FCSTD DOCUMENT  (FreeCAD 0.20R29177 +426 (Git))
Label: mechanism-sketch
License: All rights reserved
LicenseURL: http://en.wikipedia.org/wiki/All_rights_reserved
objects: Sketcher::SketchObject×1, PartDesign::Body×1
note: 2 computed .brp shape members not serialized (recipe doc carries the construction recipe); baked Part::Feature solids carry a one-line shape summary decoded from their .brp

FEATURE [Sketcher::SketchObject] Sketch
  FullyConstrained = false
  MapMode = 5
  Support = -> [XY_Plane]
  sketch-geometry (5):
    g0: LineSegment StartX=0 StartY=0 StartZ=0 EndX=77.25 EndY=-20.795 EndZ=0
    g1: LineSegment StartX=0 StartY=-310.679 StartZ=0 EndX=77.25 EndY=-20.795 EndZ=0
    g2: LineSegment StartX=0 StartY=0 StartZ=0 EndX=-77.25 EndY=20.795 EndZ=0
    g3: LineSegment StartX=-77.25 StartY=20.795 StartZ=0 EndX=-154.5 EndY=-269.088 EndZ=0
    g4: LineSegment StartX=0 StartY=-310.679 StartZ=0 EndX=-154.5 EndY=-269.088 EndZ=0
  constraints (13):
    c: Coincident(g0,g-1)
    c: PointOnObject(g1,g-2)
    c: Coincident(g1,g0)
    c: Distance(g0) = 80
    c: Distance(g1) = 300
    c: Coincident(g2,g0)
    c: Equal(g2,g0)
    c: Parallel(g2,g0)
    c: Coincident(g3,g2)
    c: Coincident(g4,g1)
    c: Coincident(g4,g3)
    c: Parallel(g2,g4)
    c: Equal(g3,g1)
FEATURE [PartDesign::Body] Body
  Group = -> [Sketch]
  Origin = -> Origin
